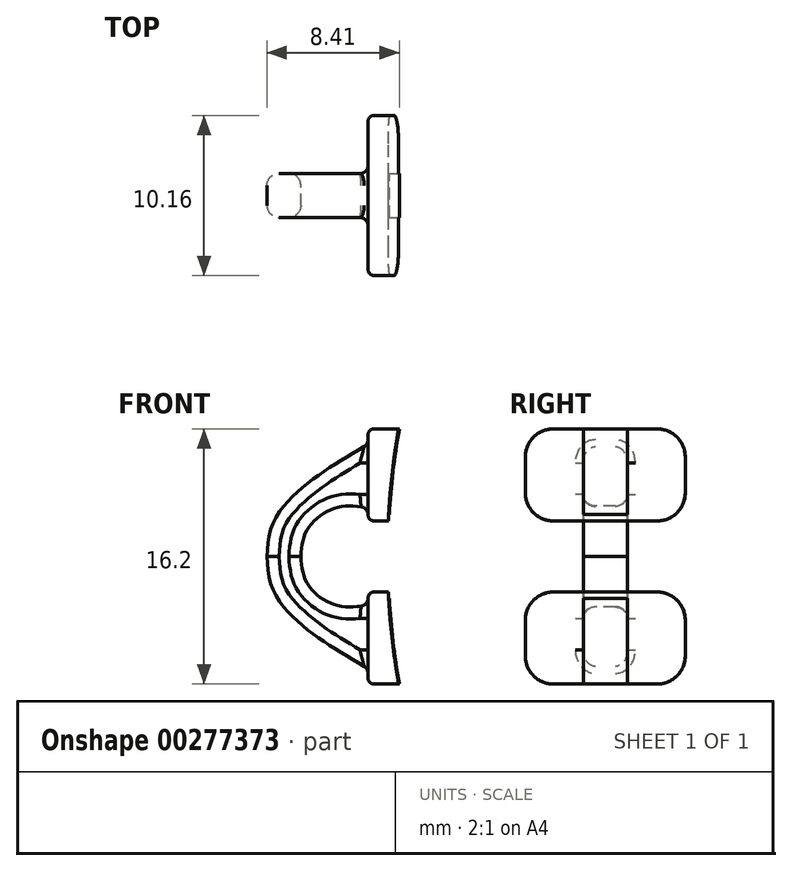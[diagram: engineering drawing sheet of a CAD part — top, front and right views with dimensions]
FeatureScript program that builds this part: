
annotation { "Feature Type Name" : "Feature", "Feature Type Description" : "" }
export const myFeature = defineFeature(function(context is Context, id is Id, definition is map)
    precondition{}
    {
        {
            var Q0;
            Q0=qCreatedBy(makeId("Front.planeOp"),FACE);
            var sketch = newSketch(context, id + "F0", { "sketchPlane" : qUnion([Q0])});
            skLineSegment(sketch, "E0", {"start": v(-29.44, -8.1) * mm, "end": v(-31.43, -8.1) * mm});
            skLineSegment(sketch, "E1", {"start": v(-31.43, -8.1) * mm, "end": v(-31.43, -7.13) * mm});
            skFitSpline(sketch, "E2", {"points": [v(-31.43, -7.13) * mm, v(-35.43, -4.51) * mm, v(-37.48, -2.1) * mm, v(-37.85, 0) * mm], "startDerivative": vector(-10.54, 6.3) * mm, "endDerivative": vector(-0.39, 7.85) * mm});
            skFitSpline(sketch, "E3", {"points": [v(-31.43, -3.1) * mm, v(-33.44, -3.1) * mm, v(-35.28, -1.74) * mm, v(-35.7, 0) * mm], "startDerivative": vector(-5.94, -0.88) * mm, "endDerivative": vector(-0.43, 5.69) * mm});
            skLineSegment(sketch, "E4", {"start": v(-31.43, -2.66) * mm, "end": v(-30.08, -2.66) * mm});
            skLineSegment(sketch, "E5.trimOffspring", {"start": v(-31.43, -3.1) * mm, "end": v(-31.43, -2.66) * mm});
            skLineSegment(sketch, "E6.MirrorCS", {"start": v(-31.43, 3.1) * mm, "end": v(-31.43, 2.66) * mm});
            skLineSegment(sketch, "E7.MirrorCS", {"start": v(-31.43, 8.1) * mm, "end": v(-31.43, 7.13) * mm});
            skLineSegment(sketch, "E8.MirrorCS", {"start": v(-29.44, 8.1) * mm, "end": v(-31.43, 8.1) * mm});
            skFitSpline(sketch, "E9.MirrorCS", {"points": [v(-31.43, 7.13) * mm, v(-35.43, 4.51) * mm, v(-37.48, 2.1) * mm, v(-37.85, 0) * mm], "startDerivative": vector(-10.54, -6.3) * mm, "endDerivative": vector(-0.39, -7.85) * mm});
            skFitSpline(sketch, "E10.MirrorCS", {"points": [v(-31.43, 3.1) * mm, v(-33.44, 3.1) * mm, v(-35.28, 1.74) * mm, v(-35.7, 0) * mm], "startDerivative": vector(-5.94, 0.88) * mm, "endDerivative": vector(-0.43, -5.69) * mm});
            skLineSegment(sketch, "E11.MirrorCS", {"start": v(-31.43, 2.66) * mm, "end": v(-30.08, 2.66) * mm});
            skPoint(sketch, "E12.orphan", {"position": v(-29, 2.66) * mm});
            skPoint(sketch, "E13.orphan", {"position": v(-29, 8.1) * mm});
            skPoint(sketch, "E14.end.orphan", {"position": v(-29, -8.1) * mm});
            skPoint(sketch, "E14.start.orphan", {"position": v(-29, -2.66) * mm});
            skArc(sketch, "E15", {"start": v(-29.44, 8.1) * mm, "mid": v(-29.84, 5.39) * mm, "end": v(-30.08, 2.66) * mm});
            skArc(sketch, "E16.trimOffspring", {"start": v(-30.08, -2.66) * mm, "mid": v(-29.84, -5.39) * mm, "end": v(-29.44, -8.1) * mm});
            skSolve(sketch);
        }
        {
            var Q0;
            Q0=qSketchRegion(id+"F0",true);
            extrude(context, id + "F1", {"entities" : qUnion([Q0]), "depth" : 2.8 * mm, "symmetric" : true});
        }
        {
            var Q0;
            Q0=qCreatedBy(makeId("Front.planeOp"),FACE);
            var sketch = newSketch(context, id + "F2", { "sketchPlane" : qUnion([Q0])});
            skLineSegment(sketch, "E17.bottom", {"start": v(-31.43, 8.1) * mm, "end": v(-29.48, 8.1) * mm});
            skLineSegment(sketch, "E17.top", {"start": v(-31.43, -8.1) * mm, "end": v(-29.48, -8.1) * mm});
            skLineSegment(sketch, "E17.left", {"start": v(-31.43, 8.1) * mm, "end": v(-31.43, 2.26) * mm});
            skLineSegment(sketch, "E18", {"start": v(-31.43, 2.26) * mm, "end": v(-30.14, 2.26) * mm});
            skLineSegment(sketch, "E19", {"start": v(-31.43, -2.26) * mm, "end": v(-30.14, -2.26) * mm});
            skLineSegment(sketch, "E20.trimOffspring", {"start": v(-31.43, -2.26) * mm, "end": v(-31.43, -8.1) * mm});
            skArc(sketch, "E21", {"start": v(-29.48, 8.1) * mm, "mid": v(-29.9, 5.2) * mm, "end": v(-30.14, 2.26) * mm});
            skArc(sketch, "E22.trimOffspring", {"start": v(-30.14, -2.26) * mm, "mid": v(-29.9, -5.2) * mm, "end": v(-29.48, -8.1) * mm});
            skSolve(sketch);
        }
        {
            var Q0;
            Q0=qSketchRegion(id+"F2",true);
            extrude(context, id + "F3", {"entities" : qUnion([Q0]), "operationType" : NewBodyOperationType.ADD, "depth" : 10.16 * mm, "symmetric" : true});
        }
        {
            var Q0;
            Q0=makeQuery(id+"F3.opExtrude","CAP_EDGE",EDGE,{"disambiguationData":[OSD([sQuery(id+"F2.wireOp",EDGE,"E17.bottom")])],"isStart":false});
            var Q1;
            Q1=makeQuery(id+"F3.opExtrude","CAP_EDGE",EDGE,{"disambiguationData":[OSD([sQuery(id+"F2.wireOp",EDGE,"E18")])],"isStart":false});
            var Q2;
            Q2=makeQuery(id+"F3.opExtrude","CAP_EDGE",EDGE,{"disambiguationData":[OSD([sQuery(id+"F2.wireOp",EDGE,"E17.bottom")])],"isStart":true});
            var Q3;
            Q3=makeQuery(id+"F3.opExtrude","CAP_EDGE",EDGE,{"disambiguationData":[OSD([sQuery(id+"F2.wireOp",EDGE,"E18")])],"isStart":true});
            var Q4;
            Q4=makeQuery(id+"F3.opExtrude","CAP_EDGE",EDGE,{"disambiguationData":[OSD([sQuery(id+"F2.wireOp",EDGE,"E19")])],"isStart":true});
            var Q5;
            Q5=makeQuery(id+"F3.opExtrude","CAP_EDGE",EDGE,{"disambiguationData":[OSD([sQuery(id+"F2.wireOp",EDGE,"E17.top")])],"isStart":true});
            var Q6;
            Q6=makeQuery(id+"F3.opExtrude","CAP_EDGE",EDGE,{"disambiguationData":[OSD([sQuery(id+"F2.wireOp",EDGE,"E17.top")])],"isStart":false});
            var Q7;
            Q7=makeQuery(id+"F3.opExtrude","CAP_EDGE",EDGE,{"disambiguationData":[OSD([sQuery(id+"F2.wireOp",EDGE,"E19")])],"isStart":false});
            fillet(context, id + "F4", {"entities" : qUnion([Q0, Q1, Q2, Q3, Q4, Q5, Q6, Q7]), "radius" : 1.78 * mm, "tangentPropagation" : true, "allowEdgeOverflow" : false});
        }
        {
            var Q0;
            Q0=makeQuery(id+"F1.opExtrude","CAP_EDGE",EDGE,{"disambiguationData":[OSD([sQuery(id+"F0.wireOp",EDGE,"E2")])],"isStart":false});
            var Q1;
            Q1=makeQuery(id+"F1.opExtrude","CAP_EDGE",EDGE,{"disambiguationData":[OSD([sQuery(id+"F0.wireOp",EDGE,"E9.MirrorCS")])],"isStart":false});
            var Q2;
            Q2=makeQuery(id+"F1.opExtrude","CAP_EDGE",EDGE,{"disambiguationData":[OSD([sQuery(id+"F0.wireOp",EDGE,"E9.MirrorCS")])],"isStart":true});
            var Q3;
            Q3=makeQuery(id+"F1.opExtrude","CAP_EDGE",EDGE,{"disambiguationData":[OSD([sQuery(id+"F0.wireOp",EDGE,"E2")])],"isStart":true});
            var Q4;
            Q4=makeQuery(id+"F1.opExtrude","CAP_EDGE",EDGE,{"disambiguationData":[OSD([sQuery(id+"F0.wireOp",EDGE,"E3")])],"isStart":false});
            var Q5;
            Q5=makeQuery(id+"F1.opExtrude","CAP_EDGE",EDGE,{"disambiguationData":[OSD([sQuery(id+"F0.wireOp",EDGE,"E10.MirrorCS")])],"isStart":false});
            var Q6;
            Q6=makeQuery(id+"F1.opExtrude","CAP_EDGE",EDGE,{"disambiguationData":[OSD([sQuery(id+"F0.wireOp",EDGE,"E3")])],"isStart":true});
            var Q7;
            Q7=makeQuery(id+"F1.opExtrude","CAP_EDGE",EDGE,{"disambiguationData":[OSD([sQuery(id+"F0.wireOp",EDGE,"E10.MirrorCS")])],"isStart":true});
            fillet(context, id + "F5", {"entities" : qUnion([Q0, Q1, Q2, Q3, Q4, Q5, Q6, Q7]), "radius" : 0.76 * mm, "tangentPropagation" : true, "allowEdgeOverflow" : false});
        }
        {
            var Q0;
            Q0=makeQuery(id+"F5.opFillet","BLEND_EDGE",EDGE,{"blendedFrom":[makeQuery(id+"F1.opExtrude","CAP_EDGE",EDGE,{"disambiguationData":[OSD([sQuery(id+"F0.wireOp",EDGE,"E10.MirrorCS")])],"isStart":false}),makeQuery(id+"F3.boolean.opBoolean","MERGE",FACE,{"derivedFrom":[makeQuery(id+"F1.opExtrude","SWEPT_FACE",FACE,{"disambiguationData":[OSD([sQuery(id+"F0.wireOp",EDGE,"E6.MirrorCS")])]}),makeQuery(id+"F1.opExtrude","SWEPT_FACE",FACE,{"disambiguationData":[OSD([sQuery(id+"F0.wireOp",EDGE,"E7.MirrorCS")])]}),makeQuery(id+"F3.opExtrude","SWEPT_FACE",FACE,{"disambiguationData":[OSD([sQuery(id+"F2.wireOp",EDGE,"E17.left")])]})]})],"blendedInto":[makeQuery(id+"F3.boolean.opBoolean","MERGE",FACE,{"derivedFrom":[makeQuery(id+"F1.opExtrude","SWEPT_FACE",FACE,{"disambiguationData":[OSD([sQuery(id+"F0.wireOp",EDGE,"E6.MirrorCS")])]}),makeQuery(id+"F1.opExtrude","SWEPT_FACE",FACE,{"disambiguationData":[OSD([sQuery(id+"F0.wireOp",EDGE,"E7.MirrorCS")])]}),makeQuery(id+"F3.opExtrude","SWEPT_FACE",FACE,{"disambiguationData":[OSD([sQuery(id+"F2.wireOp",EDGE,"E17.left")])]})]})]});
            var Q1;
            Q1=makeQuery(id+"F3.boolean.opBoolean","INTERSECT",EDGE,{"derivedFrom":[makeQuery(id+"F1.opExtrude","CAP_FACE",FACE,{"disambiguationData":[OSD([sQuery(id+"F0.wireOp",EDGE,"E0"),sQuery(id+"F0.wireOp",EDGE,"E1"),sQuery(id+"F0.wireOp",EDGE,"E2"),sQuery(id+"F0.wireOp",EDGE,"E3"),sQuery(id+"F0.wireOp",EDGE,"E4"),sQuery(id+"F0.wireOp",EDGE,"E5.trimOffspring"),sQuery(id+"F0.wireOp",EDGE,"E6.MirrorCS"),sQuery(id+"F0.wireOp",EDGE,"E7.MirrorCS"),sQuery(id+"F0.wireOp",EDGE,"E8.MirrorCS"),sQuery(id+"F0.wireOp",EDGE,"E9.MirrorCS"),sQuery(id+"F0.wireOp",EDGE,"E10.MirrorCS"),sQuery(id+"F0.wireOp",EDGE,"E11.MirrorCS"),sQuery(id+"F0.wireOp",EDGE,"YPmfCHMG-XVIC-nbxh-loHK-GwVzSPm4SBvZ"),sQuery(id+"F0.wireOp",EDGE,"8e6f791d-0f4a-4d6e-afe4-d14939ce7773.trimOffspring")])],"isStart":false}),makeQuery(id+"F3.opExtrude","SWEPT_FACE",FACE,{"disambiguationData":[OSD([sQuery(id+"F2.wireOp",EDGE,"E20.trimOffspring")])]})]});
            fillet(context, id + "F6", {"entities" : qUnion([Q0, Q1]), "radius" : 0.5 * mm, "tangentPropagation" : true, "allowEdgeOverflow" : false});
        }
        {
            var Q0;
            Q0=makeQuery(id+"F3.opExtrude","SWEPT_EDGE",EDGE,{"disambiguationData":[OSD([sQuery(id+"F2.wireOp",EDGE,"E17.left"),sQuery(id+"F2.wireOp",EDGE,"E18")])]});
            var Q1;
            Q1=makeQuery(id+"F4.opFillet","BLEND_EDGE",EDGE,{"blendedFrom":[makeQuery(id+"F3.opExtrude","CAP_EDGE",EDGE,{"disambiguationData":[OSD([sQuery(id+"F2.wireOp",EDGE,"E18")])],"isStart":true}),makeQuery(id+"F3.boolean.opBoolean","MERGE",FACE,{"derivedFrom":[makeQuery(id+"F1.opExtrude","SWEPT_FACE",FACE,{"disambiguationData":[OSD([sQuery(id+"F0.wireOp",EDGE,"E6.MirrorCS")])]}),makeQuery(id+"F1.opExtrude","SWEPT_FACE",FACE,{"disambiguationData":[OSD([sQuery(id+"F0.wireOp",EDGE,"E7.MirrorCS")])]}),makeQuery(id+"F3.opExtrude","SWEPT_FACE",FACE,{"disambiguationData":[OSD([sQuery(id+"F2.wireOp",EDGE,"E17.left")])]})]})],"blendedInto":[makeQuery(id+"F3.boolean.opBoolean","MERGE",FACE,{"derivedFrom":[makeQuery(id+"F1.opExtrude","SWEPT_FACE",FACE,{"disambiguationData":[OSD([sQuery(id+"F0.wireOp",EDGE,"E6.MirrorCS")])]}),makeQuery(id+"F1.opExtrude","SWEPT_FACE",FACE,{"disambiguationData":[OSD([sQuery(id+"F0.wireOp",EDGE,"E7.MirrorCS")])]}),makeQuery(id+"F3.opExtrude","SWEPT_FACE",FACE,{"disambiguationData":[OSD([sQuery(id+"F2.wireOp",EDGE,"E17.left")])]})]})]});
            var Q2;
            Q2=makeQuery(id+"F3.opExtrude","CAP_EDGE",EDGE,{"disambiguationData":[OSD([sQuery(id+"F2.wireOp",EDGE,"E17.left")])],"isStart":true});
            var Q3;
            Q3=makeQuery(id+"F4.opFillet","BLEND_EDGE",EDGE,{"blendedFrom":[makeQuery(id+"F3.opExtrude","CAP_EDGE",EDGE,{"disambiguationData":[OSD([sQuery(id+"F2.wireOp",EDGE,"E17.bottom")])],"isStart":true}),makeQuery(id+"F3.boolean.opBoolean","MERGE",FACE,{"derivedFrom":[makeQuery(id+"F1.opExtrude","SWEPT_FACE",FACE,{"disambiguationData":[OSD([sQuery(id+"F0.wireOp",EDGE,"E6.MirrorCS")])]}),makeQuery(id+"F1.opExtrude","SWEPT_FACE",FACE,{"disambiguationData":[OSD([sQuery(id+"F0.wireOp",EDGE,"E7.MirrorCS")])]}),makeQuery(id+"F3.opExtrude","SWEPT_FACE",FACE,{"disambiguationData":[OSD([sQuery(id+"F2.wireOp",EDGE,"E17.left")])]})]})],"blendedInto":[makeQuery(id+"F3.boolean.opBoolean","MERGE",FACE,{"derivedFrom":[makeQuery(id+"F1.opExtrude","SWEPT_FACE",FACE,{"disambiguationData":[OSD([sQuery(id+"F0.wireOp",EDGE,"E6.MirrorCS")])]}),makeQuery(id+"F1.opExtrude","SWEPT_FACE",FACE,{"disambiguationData":[OSD([sQuery(id+"F0.wireOp",EDGE,"E7.MirrorCS")])]}),makeQuery(id+"F3.opExtrude","SWEPT_FACE",FACE,{"disambiguationData":[OSD([sQuery(id+"F2.wireOp",EDGE,"E17.left")])]})]})]});
            var Q4;
            Q4=makeQuery(id+"F3.opExtrude","CAP_EDGE",EDGE,{"disambiguationData":[OSD([sQuery(id+"F2.wireOp",EDGE,"E17.left")])],"isStart":true});
            var Q5;
            Q5=makeQuery(id+"F3.boolean.opBoolean","MERGE",EDGE,{"derivedFrom":[makeQuery(id+"F1.opExtrude","SWEPT_EDGE",EDGE,{"disambiguationData":[OSD([sQuery(id+"F0.wireOp",EDGE,"E7.MirrorCS"),sQuery(id+"F0.wireOp",EDGE,"E8.MirrorCS")])]}),makeQuery(id+"F3.opExtrude","SWEPT_EDGE",EDGE,{"disambiguationData":[OSD([sQuery(id+"F2.wireOp",EDGE,"E17.bottom"),sQuery(id+"F2.wireOp",EDGE,"E17.left")])]})]});
            var Q6;
            Q6=makeQuery(id+"F3.opExtrude","SWEPT_EDGE",EDGE,{"disambiguationData":[OSD([sQuery(id+"F2.wireOp",EDGE,"E19"),sQuery(id+"F2.wireOp",EDGE,"E20.trimOffspring")])]});
            fillet(context, id + "F7", {"entities" : qUnion([Q0, Q1, Q2, Q3, Q4, Q5, Q6]), "radius" : 0.38 * mm, "tangentPropagation" : true, "allowEdgeOverflow" : false});
        }
    });
